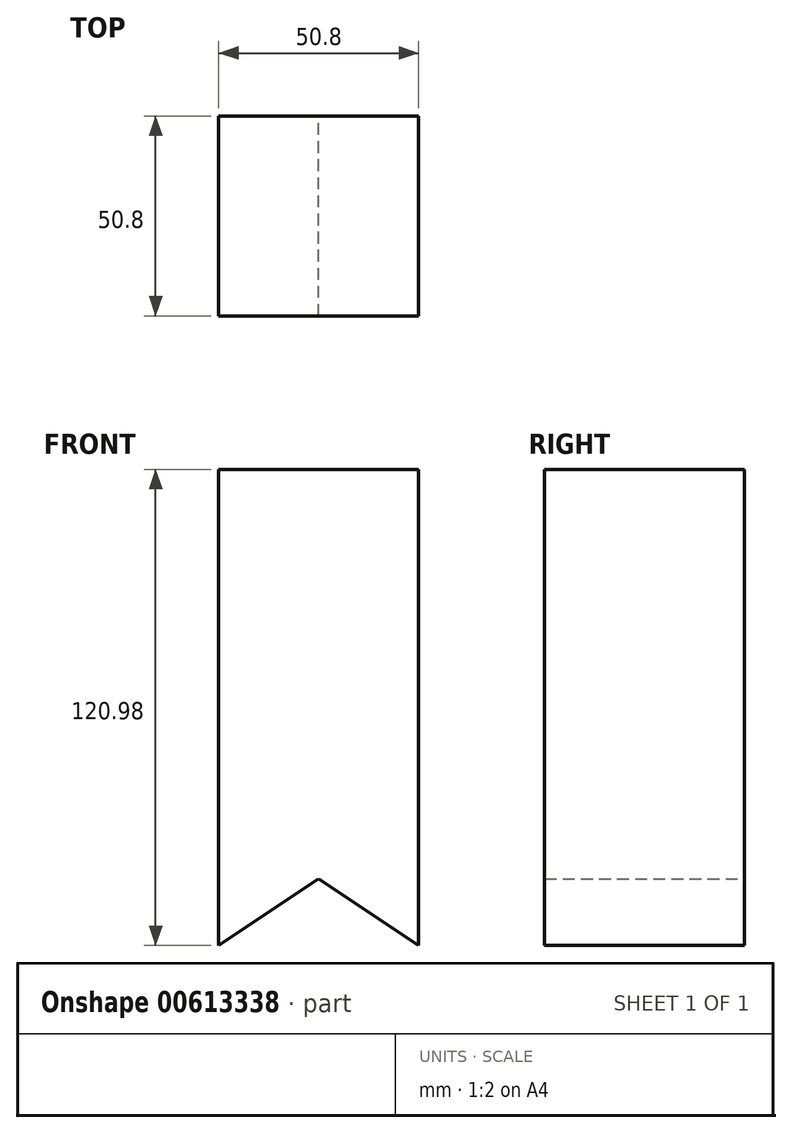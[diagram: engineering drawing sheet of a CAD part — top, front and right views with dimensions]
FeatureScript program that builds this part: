
annotation { "Feature Type Name" : "Feature", "Feature Type Description" : "" }
export const myFeature = defineFeature(function(context is Context, id is Id, definition is map)
    precondition{}
    {
        {
            var Q0;
            Q0=qCreatedBy(makeId("Front.planeOp"),FACE);
            var sketch = newSketch(context, id + "F0", { "sketchPlane" : qUnion([Q0])});
            skLineSegment(sketch, "E0.bottom", {"start": v(25.4, 60.49) * mm, "end": v(-25.4, 60.49) * mm});
            skLineSegment(sketch, "E0.left", {"start": v(25.4, 60.49) * mm, "end": v(25.4, -60.49) * mm});
            skLineSegment(sketch, "E0.right", {"start": v(-25.4, 60.49) * mm, "end": v(-25.4, -60.49) * mm});
            skPoint(sketch, "E0.middle", {"position": v(0, 0) * mm});
            skLineSegment(sketch, "E1", {"start": v(-25.4, -60.49) * mm, "end": v(0, -43.56) * mm});
            skLineSegment(sketch, "E2", {"start": v(25.4, -60.49) * mm, "end": v(0, -43.56) * mm});
            skSolve(sketch);
        }
        {
            var Q0;
            Q0 = qSketchRegion(id + "F0", true);
            extrude(context, id + "F1", {"entities" : qUnion([Q0]), "depth" : 50.8 * mm, "offsetDistance" : 25.4 * mm});
        }
    });
